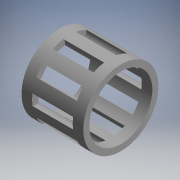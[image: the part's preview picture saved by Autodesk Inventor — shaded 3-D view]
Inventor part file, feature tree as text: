
AUTODESK INVENTOR PART (.ipt)
format: ipt  version: 2017.3 (Build 213256000, 256)  size: 153,088 bytes
history: native  units: mm (DEFAULTED — no unit token found)
features: other x77, revolve x2, sketch x2, pattern_circular x1
ambient origin geometry x8: Origin, YZ Plane, XZ Plane, XY Plane, X Axis, Y Axis, Z Axis, Center Point
bodies: Solid1 (feature_tree)
feature tree (82):
  revolve  "Revolution1"  Angle=360.0deg
  revolve  "Revolution2"  [1 undecoded]
  pattern_circular  "Circular Pattern1"  [2 undecoded]
  other  "IP_1_XY"
  other  "IP_1_YZ"
  other  "IP_1_ZX"
  other  "IP_1_X"
  other  "IP_1_Y"
  other  "IP_1_Z"
  other  "IP_1_Center"
  other  "IP_3_1_XY"
  other  "IP_3_1_YZ"
  other  "IP_3_1_ZX"
  other  "IP_3_1_X"
  other  "IP_3_1_Y"
  other  "IP_3_1_Z"
  other  "IP_3_1_Center"
  other  "IP_3_10_XY"
  other  "IP_3_10_YZ"
  other  "IP_3_10_ZX"
  other  "IP_3_10_X"
  other  "IP_3_10_Y"
  other  "IP_3_10_Z"
  other  "IP_3_10_Center"
  other  "IP_3_2_XY"
  other  "IP_3_2_YZ"
  other  "IP_3_2_ZX"
  other  "IP_3_2_X"
  other  "IP_3_2_Y"
  other  "IP_3_2_Z"
  other  "IP_3_2_Center"
  other  "IP_3_3_XY"
  other  "IP_3_3_YZ"
  other  "IP_3_3_ZX"
  other  "IP_3_3_X"
  other  "IP_3_3_Y"
  other  "IP_3_3_Z"
  other  "IP_3_3_Center"
  other  "IP_3_4_XY"
  other  "IP_3_4_YZ"
  other  "IP_3_4_ZX"
  other  "IP_3_4_X"
  other  "IP_3_4_Y"
  other  "IP_3_4_Z"
  other  "IP_3_4_Center"
  other  "IP_3_5_XY"
  other  "IP_3_5_YZ"
  other  "IP_3_5_ZX"
  other  "IP_3_5_X"
  other  "IP_3_5_Y"
  other  "IP_3_5_Z"
  other  "IP_3_5_Center"
  other  "IP_3_6_XY"
  other  "IP_3_6_YZ"
  other  "IP_3_6_ZX"
  other  "IP_3_6_X"
  other  "IP_3_6_Y"
  other  "IP_3_6_Z"
  other  "IP_3_6_Center"
  other  "IP_3_7_XY"
  other  "IP_3_7_YZ"
  other  "IP_3_7_ZX"
  other  "IP_3_7_X"
  other  "IP_3_7_Y"
  other  "IP_3_7_Z"
  other  "IP_3_7_Center"
  other  "IP_3_8_XY"
  other  "IP_3_8_YZ"
  other  "IP_3_8_ZX"
  other  "IP_3_8_X"
  other  "IP_3_8_Y"
  other  "IP_3_8_Z"
  other  "IP_3_8_Center"
  other  "IP_3_9_XY"
  other  "IP_3_9_YZ"
  other  "IP_3_9_ZX"
  other  "IP_3_9_X"
  other  "IP_3_9_Y"
  other  "IP_3_9_Z"
  other  "IP_3_9_Center"
  sketch  "Sketch_1"  dims[d0=360.0deg d1=360.0deg]
  sketch  "Sketch_2"  dims[d2=100.0mm d3=6.283185mm]
note: 3 required parameter values undecoded (feature->parameter linkage not recoverable at this tier; creation-order binding heuristic only, values carry confidence <= 0.55)
